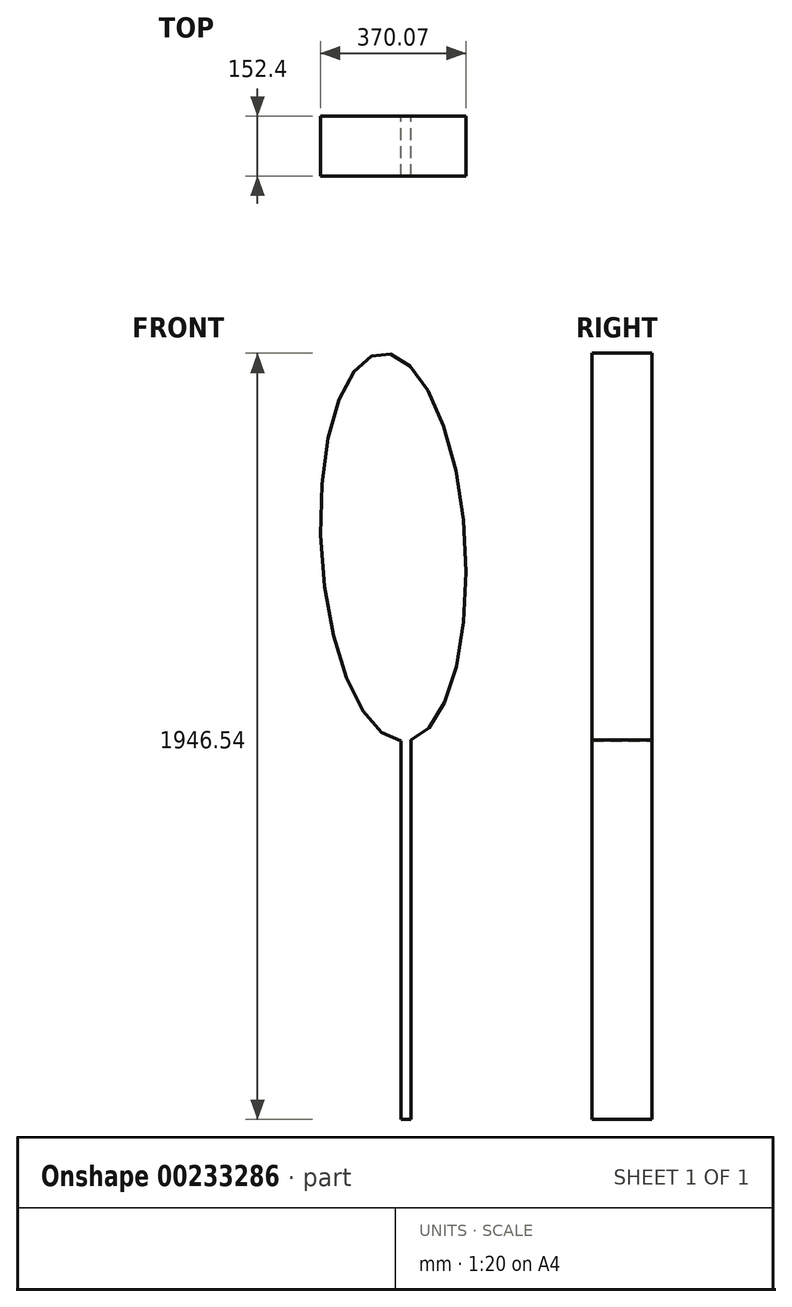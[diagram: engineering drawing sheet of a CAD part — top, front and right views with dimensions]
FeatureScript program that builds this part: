
annotation { "Feature Type Name" : "Feature", "Feature Type Description" : "" }
export const myFeature = defineFeature(function(context is Context, id is Id, definition is map)
    precondition{}
    {
        {
            var Q0;
            Q0=qCreatedBy(makeId("Front.planeOp"),FACE);
            var sketch = newSketch(context, id + "F0", { "sketchPlane" : qUnion([Q0])});
            skLineSegment(sketch, "E0.bottom", {"start": v(0.7, 487.17) * mm, "end": v(-24.7, 487.17) * mm});
            skLineSegment(sketch, "E0.top", {"start": v(0.7, -512.83) * mm, "end": v(-24.7, -512.83) * mm});
            skLineSegment(sketch, "E0.left", {"start": v(0.7, 487.17) * mm, "end": v(0.7, -512.83) * mm});
            skLineSegment(sketch, "E0.right", {"start": v(-24.7, 487.17) * mm, "end": v(-24.7, -512.83) * mm});
            skEllipse(sketch, "E1", {"center": v(-43.57, 940.8) * mm, "majorRadius": 493.63 * mm, "minorRadius": 183.12 * mm, "majorAxis": v(0.06, -1)});
            skSolve(sketch);
        }
        {
            var Q0;
            Q0 = qSketchRegion(id + "F0", true);
            extrude(context, id + "F1", {"entities" : qUnion([Q0]), "depth" : 152.4 * mm});
        }
    });
